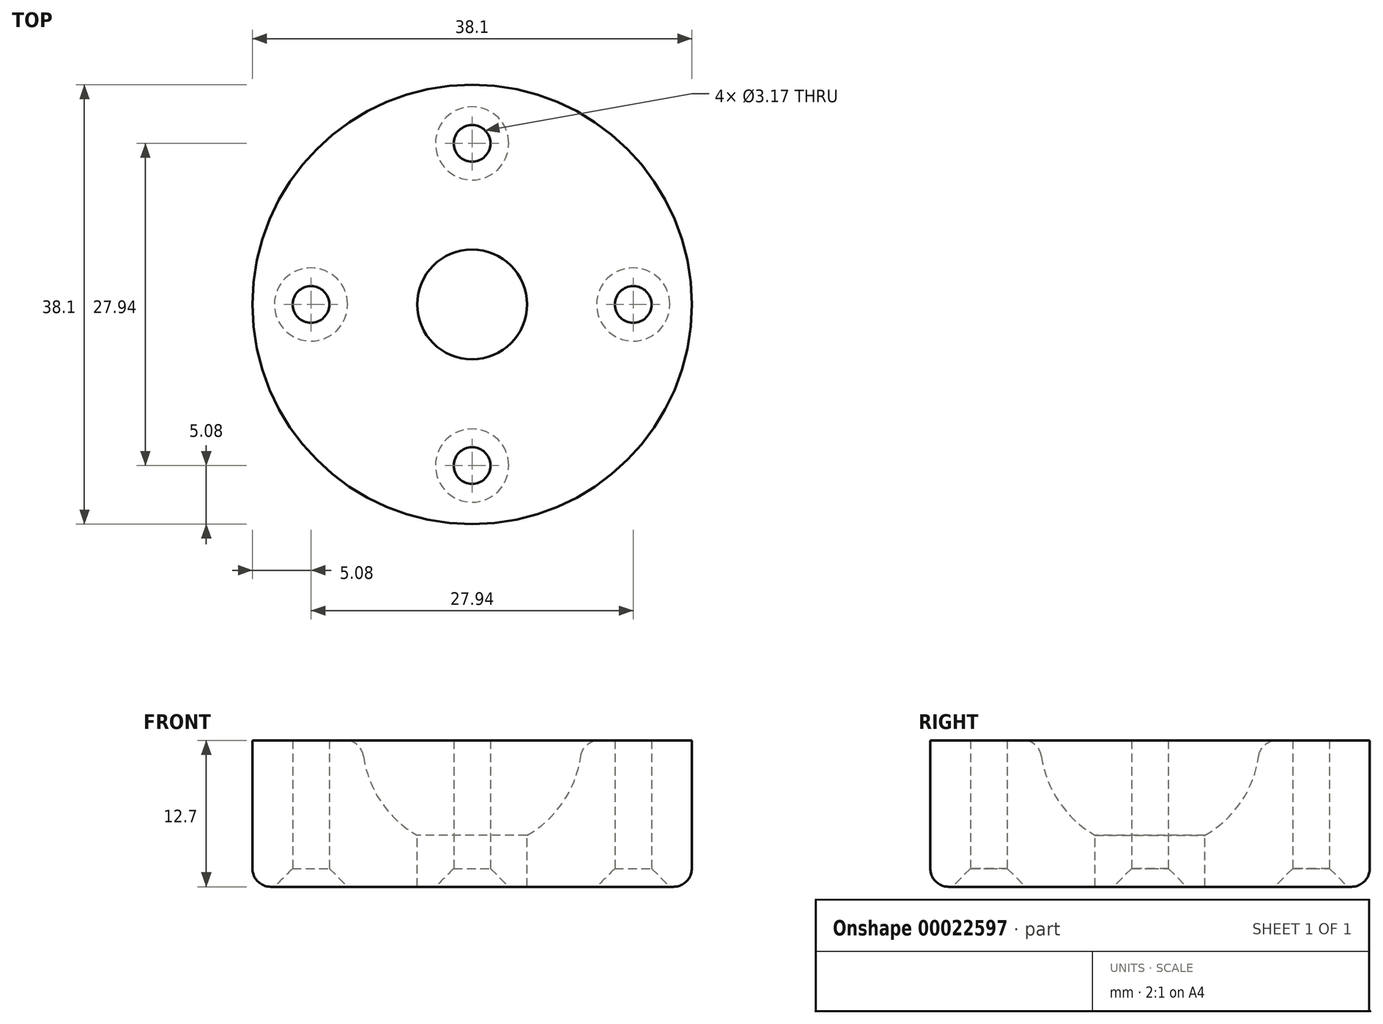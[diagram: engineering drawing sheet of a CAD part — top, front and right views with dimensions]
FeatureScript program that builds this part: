
annotation { "Feature Type Name" : "Feature", "Feature Type Description" : "" }
export const myFeature = defineFeature(function(context is Context, id is Id, definition is map)
    precondition{}
    {
        {
            var Q0;
            Q0=qCreatedBy(makeId("Front.planeOp"),FACE);
            var sketch = newSketch(context, id + "F0", { "sketchPlane" : qUnion([Q0])});
            skLineSegment(sketch, "E0.bottom", {"start": v(19.05, -6.35) * mm, "end": v(4.76, -6.35) * mm});
            skLineSegment(sketch, "E0.top", {"start": v(19.05, 6.35) * mm, "end": v(9.53, 6.35) * mm});
            skLineSegment(sketch, "E0.left", {"start": v(19.05, -6.35) * mm, "end": v(19.05, 6.35) * mm});
            skPoint(sketch, "E0.middle", {"position": v(0, 0) * mm});
            skArc(sketch, "E1", {"start": v(4.76, -1.9) * mm, "mid": v(8.25, 1.59) * mm, "end": v(9.53, 6.35) * mm});
            skLineSegment(sketch, "E2.left", {"start": v(4.76, -6.35) * mm, "end": v(4.76, -1.9) * mm});
            skPoint(sketch, "E2.middle", {"position": v(0, -3.17) * mm});
            skLineSegment(sketch, "E3", {"start": v(0, 0) * mm, "end": v(0, -6.35) * mm});
            skPoint(sketch, "E0.right.end.orphan", {"position": v(-19.05, 6.35) * mm});
            skPoint(sketch, "E4.orphan", {"position": v(-19.05, -6.35) * mm});
            skPoint(sketch, "E5.orphan", {"position": v(0, 15.88) * mm});
            skPoint(sketch, "E2.right.end.orphan", {"position": v(-4.76, 0) * mm});
            skPoint(sketch, "E6.orphan", {"position": v(4.76, 0) * mm});
            skPoint(sketch, "E7.orphan", {"position": v(-4.76, -6.35) * mm});
            skSolve(sketch);
        }
        {
            var Q0;
            Q0=makeQuery(id+"F0.imprint","IMPRINT",FACE,{"disambiguationData":[TD([[makeQuery(id+"F0.imprint","IMPRINT",EDGE,{"derivedFrom":sQuery(id+"F0.wireOp",EDGE,"E0.bottom")}),-1.0]])]});
            var Q1;
            Q1=sQuery(id+"F0.wireOp",EDGE,"E3");
            revolve(context, id + "F1", {"entities" : qUnion([Q0]), "axis" : qUnion([Q1]), "revolveType" : RevolveType.FULL});
        }
        {
            var Q0;
            Q0=makeQuery(id+"F1.opRevolve","SWEPT_EDGE",EDGE,{"disambiguationData":[OSD([sQuery(id+"F0.wireOp",EDGE,"E0.top"),sQuery(id+"F0.wireOp",EDGE,"E1")])]});
            var Q1;
            Q1=makeQuery(id+"F1.opRevolve","SWEPT_EDGE",EDGE,{"disambiguationData":[OSD([sQuery(id+"F0.wireOp",EDGE,"E0.bottom"),sQuery(id+"F0.wireOp",EDGE,"E0.left")])]});
            fillet(context, id + "F2", {"entities" : qUnion([Q0, Q1]), "radius" : 1.59 * mm, "tangentPropagation" : true, "allowEdgeOverflow" : false});
        }
        {
            var Q0;
            Q0=makeQuery(id+"F1.opRevolve","SWEPT_FACE",FACE,{"disambiguationData":[OSD([sQuery(id+"F0.wireOp",EDGE,"E0.bottom")])]});
            var sketch = newSketch(context, id + "F3", { "sketchPlane" : qUnion([Q0])});
            skPoint(sketch, "E8", {"position": v(0, 13.97) * mm});
            skPoint(sketch, "E9", {"position": v(13.97, 0) * mm});
            skPoint(sketch, "E10", {"position": v(0, -13.97) * mm});
            skPoint(sketch, "E11", {"position": v(-13.97, 0) * mm});
            skSolve(sketch);
        }
        {
            var Q0;
            Q0=sQuery(id+"F3.wireOp",VERTEX,"E8");
            var Q1;
            Q1=sQuery(id+"F3.wireOp",VERTEX,"E9");
            var Q2;
            Q2=sQuery(id+"F3.wireOp",VERTEX,"E10");
            var Q3;
            Q3=sQuery(id+"F3.wireOp",VERTEX,"E11");
            var Q4;
            Q4=makeQuery(id+"F1.opRevolve","SWEPT_BODY",BODY,{"disambiguationData":[OSD([sQuery(id+"F0.wireOp",EDGE,"E0.bottom"),sQuery(id+"F0.wireOp",EDGE,"E0.top"),sQuery(id+"F0.wireOp",EDGE,"E0.left"),sQuery(id+"F0.wireOp",EDGE,"E1"),sQuery(id+"F0.wireOp",EDGE,"E2.left")])]});
            hole(context, id + "F4", {"style" : HoleStyle.C_SINK, "endStyle" : HoleEndStyle.THROUGH, "holeDiameter" : 3.17 * mm, "cSinkDiameter" : 6.35 * mm, "cSinkAngle" : 90 * degree, "isTappedThrough" : true, "tappedDepth" : 12.7 * mm, "tapClearance" : 3, "locations" : qUnion([Q0, Q1, Q2, Q3]), "scope" : qUnion([Q4])});
        }
    });
